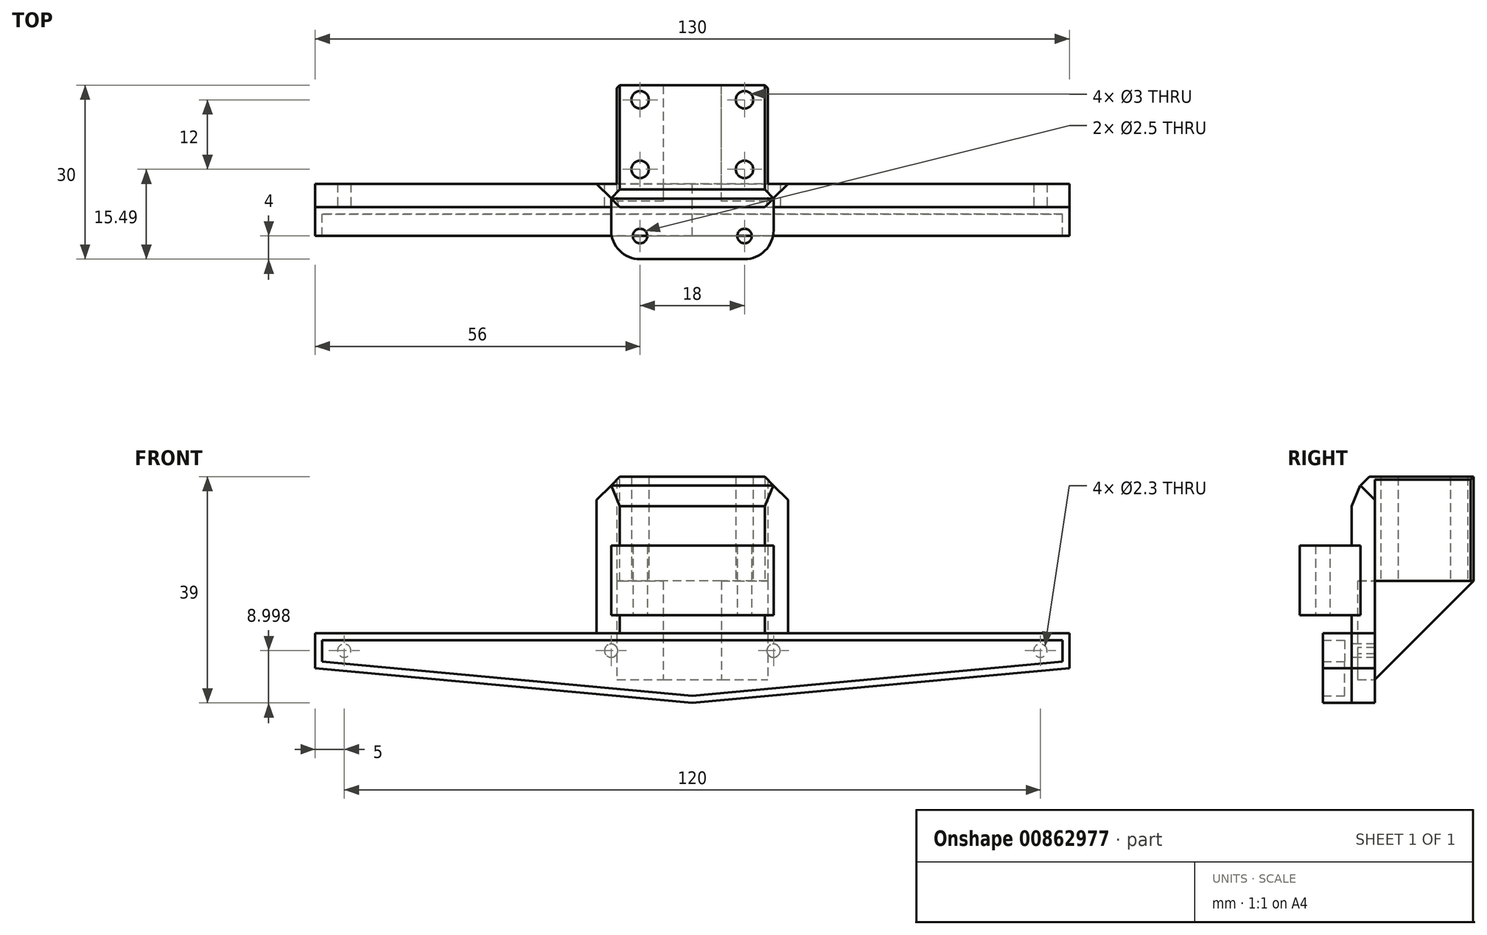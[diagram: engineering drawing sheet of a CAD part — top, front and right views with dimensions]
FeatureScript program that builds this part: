
annotation { "Feature Type Name" : "Feature", "Feature Type Description" : "" }
export const myFeature = defineFeature(function(context is Context, id is Id, definition is map)
    precondition{}
    {
        {
            var Q0;
            Q0=qCreatedBy(makeId("Top.planeOp"),FACE);
            var sketch = newSketch(context, id + "F0", { "sketchPlane" : qUnion([Q0])});
            skLineSegment(sketch, "E0.bottom", {"start": v(9, 10) * mm, "end": v(-9, 10) * mm});
            skLineSegment(sketch, "E0.top", {"start": v(9, -10) * mm, "end": v(-9, -10) * mm});
            skLineSegment(sketch, "E0.left", {"start": v(14, 5) * mm, "end": v(14, -5) * mm});
            skLineSegment(sketch, "E0.right", {"start": v(-14, 5) * mm, "end": v(-14, -5) * mm});
            skPoint(sketch, "E0.middle", {"position": v(0, 0) * mm});
            skCircle(sketch, "E1", {"center": v(-9, 6) * mm, "radius": 1.25 * mm});
            skCircle(sketch, "E2", {"center": v(9, 6) * mm, "radius": 1.25 * mm});
            skCircle(sketch, "E3", {"center": v(9, -6) * mm, "radius": 1.25 * mm});
            skCircle(sketch, "E4", {"center": v(-9, -6) * mm, "radius": 1.25 * mm});
            skPoint(sketch, "E5.visualSharp", {"position": v(-14, 10) * mm});
            skArc(sketch, "E5.filletArc", {"start": v(-9, 10) * mm, "mid": v(-12.54, 8.54) * mm, "end": v(-14, 5) * mm});
            skPoint(sketch, "E6.visualSharp", {"position": v(14, 10) * mm});
            skArc(sketch, "E6.filletArc", {"start": v(14, 5) * mm, "mid": v(12.54, 8.54) * mm, "end": v(9, 10) * mm});
            skPoint(sketch, "E7.visualSharp", {"position": v(14, -10) * mm});
            skArc(sketch, "E7.filletArc", {"start": v(9, -10) * mm, "mid": v(12.54, -8.54) * mm, "end": v(14, -5) * mm});
            skPoint(sketch, "E8.visualSharp", {"position": v(-14, -10) * mm});
            skArc(sketch, "E8.filletArc", {"start": v(-14, -5) * mm, "mid": v(-12.54, -8.54) * mm, "end": v(-9, -10) * mm});
            skSolve(sketch);
        }
        {
            var Q0;
            Q0 = qSketchRegion(id + "F0", true);
            extrude(context, id + "F1", {"entities" : qUnion([Q0]), "depth" : 12 * mm, "offsetDistance" : 25 * mm});
        }
        {
            var Q0;
            Q0=qCreatedBy(makeId("Front.planeOp"),FACE);
            var sketch = newSketch(context, id + "F2", { "sketchPlane" : qUnion([Q0])});
            skLineSegment(sketch, "E9", {"start": v(-65, -3.14) * mm, "end": v(65, -3.14) * mm});
            skLineSegment(sketch, "E10", {"start": v(65, -3.14) * mm, "end": v(65, -9.14) * mm});
            skLineSegment(sketch, "E11", {"start": v(65, -9.14) * mm, "end": v(0, -15.14) * mm});
            skLineSegment(sketch, "E12", {"start": v(0, -15.14) * mm, "end": v(-65, -9.14) * mm});
            skLineSegment(sketch, "E13", {"start": v(-65, -9.14) * mm, "end": v(-65, -3.14) * mm});
            skLineSegment(sketch, "E14", {"start": v(-17.48, -3.14) * mm, "end": v(-17.48, 23.86) * mm});
            skLineSegment(sketch, "E15", {"start": v(-17.48, 23.86) * mm, "end": v(17.48, 23.86) * mm});
            skLineSegment(sketch, "E16", {"start": v(17.48, 23.86) * mm, "end": v(17.48, -3.14) * mm});
            skLineSegment(sketch, "E17", {"start": v(-17.48, -3.14) * mm, "end": v(-17.48, -11.14) * mm});
            skLineSegment(sketch, "E18", {"start": v(-17.48, -11.14) * mm, "end": v(17.48, -11.14) * mm});
            skLineSegment(sketch, "E19", {"start": v(17.48, -11.14) * mm, "end": v(17.48, -3.14) * mm});
            skSolve(sketch);
        }
        {
            var Q0;
            Q0=makeQuery(id+"F2.imprint","IMPRINT",FACE,{"disambiguationData":[TD([[makeQuery(id+"F2.imprint","IMPRINT",EDGE,{"derivedFrom":sQuery(id+"F2.wireOp",EDGE,"E9")}),-1.0]])]});
            var Q1;
            {var subQ0=sQuery(id+"F2.wireOp",EDGE,"E14");Q1=makeQuery(id+"F2.imprint","IMPRINT",FACE,{"disambiguationData":[TD([[makeQuery(id+"F2.imprint","IMPRINT",EDGE,{"derivedFrom":subQ0}),-1.0]])]});}
            var Q2;
            {var subQ0=sQuery(id+"F2.wireOp",EDGE,"E17");Q2=makeQuery(id+"F2.imprint","IMPRINT",FACE,{"disambiguationData":[TD([[makeQuery(id+"F2.imprint","IMPRINT",EDGE,{"derivedFrom":subQ0}),1.0]])]});}
            extrude(context, id + "F3", {"entities" : qUnion([Q0, Q1, Q2]), "depth" : 1 * mm, "offsetDistance" : 25 * mm});
        }
        {
            var Q0;
            {var subQ0=sQuery(id+"F2.wireOp",EDGE,"E14");Q0=makeQuery(id+"F2.imprint","IMPRINT",FACE,{"disambiguationData":[TD([[makeQuery(id+"F2.imprint","IMPRINT",EDGE,{"derivedFrom":subQ0}),-1.0]])]});}
            var Q1;
            {var subQ0=sQuery(id+"F2.wireOp",EDGE,"E17");Q1=makeQuery(id+"F2.imprint","IMPRINT",FACE,{"disambiguationData":[TD([[makeQuery(id+"F2.imprint","IMPRINT",EDGE,{"derivedFrom":subQ0}),1.0]])]});}
            extrude(context, id + "F4", {"entities" : qUnion([Q0, Q1]), "operationType" : NewBodyOperationType.ADD, "oppositeDirection" : true, "depth" : 20 * mm, "offsetDistance" : 25 * mm});
        }
        {
            var Q0;
            Q0=makeQuery(id+"F3.opExtrude","CAP_FACE",FACE,{"disambiguationData":[OSD([sQuery(id+"F2.wireOp",EDGE,"E9"),sQuery(id+"F2.wireOp",EDGE,"E10"),sQuery(id+"F2.wireOp",EDGE,"E11"),sQuery(id+"F2.wireOp",EDGE,"E12"),sQuery(id+"F2.wireOp",EDGE,"E13"),sQuery(id+"F2.wireOp",EDGE,"E14"),sQuery(id+"F2.wireOp",EDGE,"E15"),sQuery(id+"F2.wireOp",EDGE,"E16")])],"isStart":false});
            var sketch = newSketch(context, id + "F5", { "sketchPlane" : qUnion([Q0])});
            skLineSegment(sketch, "E20", {"start": v(-65, -6.14) * mm, "end": v(65, -6.14) * mm, "construction": true});
            skCircle(sketch, "E21", {"center": v(-60, -6.14) * mm, "radius": 1.15 * mm});
            skCircle(sketch, "E22", {"center": v(60, -6.14) * mm, "radius": 1.15 * mm});
            skLineSegment(sketch, "E23", {"start": v(-55, -3.14) * mm, "end": v(-55, -10.06) * mm});
            skLineSegment(sketch, "E24", {"start": v(55, -3.14) * mm, "end": v(55, -10.06) * mm});
            skCircle(sketch, "E25", {"center": v(14, -6.14) * mm, "radius": 1.15 * mm});
            skCircle(sketch, "E26", {"center": v(-14, -6.14) * mm, "radius": 1.15 * mm});
            skSolve(sketch);
        }
        {
            var Q0;
            Q0=makeQuery(id+"F5.imprint","IMPRINT",FACE,{"disambiguationData":[TD([[makeQuery(id+"F5.imprint","IMPRINT",EDGE,{"derivedFrom":sQuery(id+"F5.wireOp",EDGE,"E21")}),-1.0]])]});
            var Q1;
            Q1=makeQuery(id+"F5.imprint","IMPRINT",FACE,{"disambiguationData":[TD([[makeQuery(id+"F5.imprint","IMPRINT",EDGE,{"derivedFrom":sQuery(id+"F5.wireOp",EDGE,"E22")}),-1.0]])]});
            var Q2;
            {var subQ0=sQuery(id+"F2.wireOp",EDGE,"E10");Q2=makeQuery(id+"F2.imprint","IMPRINT",FACE,{"disambiguationData":[TD([[makeQuery(id+"F2.imprint","IMPRINT",EDGE,{"derivedFrom":subQ0}),-1.0]])]});}
            extrude(context, id + "F6", {"entities" : qUnion([Q0, Q1, Q2]), "operationType" : NewBodyOperationType.ADD, "oppositeDirection" : true, "depth" : 3 * mm, "offsetDistance" : 25 * mm});
        }
        {
            var Q0;
            Q0=makeQuery(id+"F5.imprint","IMPRINT",FACE,{"disambiguationData":[TD([[makeQuery(id+"F5.imprint","IMPRINT",EDGE,{"derivedFrom":sQuery(id+"F5.wireOp",EDGE,"E21")}),1.0]])]});
            var Q1;
            Q1=makeQuery(id+"F5.imprint","IMPRINT",FACE,{"disambiguationData":[TD([[makeQuery(id+"F5.imprint","IMPRINT",EDGE,{"derivedFrom":sQuery(id+"F5.wireOp",EDGE,"E22")}),1.0]])]});
            extrude(context, id + "F7", {"entities" : qUnion([Q0, Q1]), "operationType" : NewBodyOperationType.REMOVE, "endBound" : BoundingType.UP_TO_NEXT, "oppositeDirection" : true, "depth" : 25 * mm, "offsetDistance" : 25 * mm});
        }
        {
            var Q0;
            Q0=makeQuery(id+"F5.imprint","IMPRINT",FACE,{"disambiguationData":[TD([[makeQuery(id+"F5.imprint","IMPRINT",EDGE,{"derivedFrom":sQuery(id+"F5.wireOp",EDGE,"E26")}),1.0]])]});
            var Q1;
            Q1=makeQuery(id+"F5.imprint","IMPRINT",FACE,{"disambiguationData":[TD([[makeQuery(id+"F5.imprint","IMPRINT",EDGE,{"derivedFrom":sQuery(id+"F5.wireOp",EDGE,"E25")}),1.0]])]});
            extrude(context, id + "F8", {"entities" : qUnion([Q0, Q1]), "operationType" : NewBodyOperationType.REMOVE, "oppositeDirection" : true, "depth" : 10 * mm, "offsetDistance" : 25 * mm});
        }
        {
            var Q0;
            Q0=makeQuery(id+"F4.opExtrude","SWEPT_FACE",FACE,{"disambiguationData":[OSD([sQuery(id+"F2.wireOp",EDGE,"E18")])]});
            var sketch = newSketch(context, id + "F9", { "sketchPlane" : qUnion([Q0])});
            skLineSegment(sketch, "E27", {"start": v(13, -20) * mm, "end": v(13, 0) * mm});
            skLineSegment(sketch, "E28", {"start": v(13, 0) * mm, "end": v(5, 0) * mm});
            skLineSegment(sketch, "E29", {"start": v(5, 0) * mm, "end": v(5, -20) * mm});
            skLineSegment(sketch, "E30", {"start": v(-5, -20) * mm, "end": v(-5, 0) * mm});
            skLineSegment(sketch, "E31", {"start": v(-5, 0) * mm, "end": v(-13, 0) * mm});
            skLineSegment(sketch, "E32", {"start": v(-13, 0) * mm, "end": v(-13, -20) * mm});
            skSolve(sketch);
        }
        {
            var Q0;
            {var subQ0=sQuery(id+"F9.wireOp",EDGE,"E27");Q0=makeQuery(id+"F9.imprint","IMPRINT",FACE,{"disambiguationData":[TD([[makeQuery(id+"F9.imprint","IMPRINT",EDGE,{"derivedFrom":subQ0}),1.0]])]});}
            var Q1;
            {var subQ0=sQuery(id+"F9.wireOp",EDGE,"E30");Q1=makeQuery(id+"F9.imprint","IMPRINT",FACE,{"disambiguationData":[TD([[makeQuery(id+"F9.imprint","IMPRINT",EDGE,{"derivedFrom":subQ0}),1.0]])]});}
            extrude(context, id + "F10", {"entities" : qUnion([Q0, Q1]), "operationType" : NewBodyOperationType.REMOVE, "oppositeDirection" : true, "depth" : 17 * mm, "offsetDistance" : 25 * mm});
        }
        {
            var Q0;
            Q0=makeQuery(id+"F10.boolean.opBoolean","COPY",FACE,{"derivedFrom":makeQuery(id+"F10.opExtrude","CAP_FACE",FACE,{"disambiguationData":[OSD([sQuery(id+"F2.wireOp",EDGE,"E18"),sQuery(id+"F9.wireOp",EDGE,"E30"),sQuery(id+"F9.wireOp",EDGE,"E31"),sQuery(id+"F9.wireOp",EDGE,"E32")])],"isStart":false})});
            var sketch = newSketch(context, id + "F11", { "sketchPlane" : qUnion([Q0])});
            skCircle(sketch, "E33", {"center": v(-9, -5.5) * mm, "radius": 1.5 * mm});
            skCircle(sketch, "E34", {"center": v(9, -5.5) * mm, "radius": 1.5 * mm});
            skCircle(sketch, "E35", {"center": v(9, -17.5) * mm, "radius": 1.5 * mm});
            skCircle(sketch, "E36", {"center": v(-9, -17.5) * mm, "radius": 1.5 * mm});
            skSolve(sketch);
        }
        {
            var Q0;
            Q0=makeQuery(id+"F11.imprint","IMPRINT",FACE,{"disambiguationData":[TD([[makeQuery(id+"F11.imprint","IMPRINT",EDGE,{"derivedFrom":sQuery(id+"F11.wireOp",EDGE,"E33")}),1.0]])]});
            var Q1;
            Q1=makeQuery(id+"F11.imprint","IMPRINT",FACE,{"disambiguationData":[TD([[makeQuery(id+"F11.imprint","IMPRINT",EDGE,{"derivedFrom":sQuery(id+"F11.wireOp",EDGE,"E36")}),1.0]])]});
            var Q2;
            Q2=makeQuery(id+"F11.imprint","IMPRINT",FACE,{"disambiguationData":[TD([[makeQuery(id+"F11.imprint","IMPRINT",EDGE,{"derivedFrom":sQuery(id+"F11.wireOp",EDGE,"E34")}),1.0]])]});
            var Q3;
            Q3=makeQuery(id+"F11.imprint","IMPRINT",FACE,{"disambiguationData":[TD([[makeQuery(id+"F11.imprint","IMPRINT",EDGE,{"derivedFrom":sQuery(id+"F11.wireOp",EDGE,"E35")}),1.0]])]});
            extrude(context, id + "F12", {"entities" : qUnion([Q0, Q1, Q2, Q3]), "operationType" : NewBodyOperationType.REMOVE, "endBound" : BoundingType.UP_TO_NEXT, "oppositeDirection" : true, "depth" : 25 * mm, "offsetDistance" : 25 * mm});
        }
        {
            var Q0;
            {var subQ4=sQuery(id+"F5.wireOp",EDGE,"E23");Q0=makeQuery(id+"F5.imprint","IMPRINT",FACE,{"disambiguationData":[TD([[makeQuery(id+"F5.imprint","IMPRINT",EDGE,{"derivedFrom":subQ4}),1.0]])]});}
            var sketch = newSketch(context, id + "F13", { "sketchPlane" : qUnion([Q0])});
            skLineSegment(sketch, "E37", {"start": v(-65, -2.43) * mm, "end": v(65, -2.43) * mm});
            skLineSegment(sketch, "E38", {"start": v(65, -2.43) * mm, "end": v(65, -8.43) * mm});
            skLineSegment(sketch, "E39", {"start": v(65, -8.43) * mm, "end": v(0, -14.43) * mm});
            skLineSegment(sketch, "E40", {"start": v(0, -14.43) * mm, "end": v(-65, -8.43) * mm});
            skLineSegment(sketch, "E41", {"start": v(-65, -8.43) * mm, "end": v(-65, -2.43) * mm});
            skSolve(sketch);
        }
        {
            var Q0;
            Q0 = qSketchRegion(id + "F13", true);
            extrude(context, id + "F14", {"entities" : qUnion([Q0]), "depth" : 5 * mm, "offsetDistance" : 25 * mm});
        }
        {
            var Q0;
            Q0=makeQuery(id+"F14.opExtrude","CAP_FACE",FACE,{"disambiguationData":[OSD([sQuery(id+"F13.wireOp",EDGE,"E37"),sQuery(id+"F13.wireOp",EDGE,"E38"),sQuery(id+"F13.wireOp",EDGE,"E39"),sQuery(id+"F13.wireOp",EDGE,"E40"),sQuery(id+"F13.wireOp",EDGE,"E41")])],"isStart":false});
            shell(context, id + "F15", {"entities" : qUnion([Q0]), "thickness" : 1.2 * mm});
        }
        {
            var Q0;
            Q0=makeQuery(id+"F15.opShell","OFFSET_FACE",FACE,{"disambiguationData":[OSD([sQuery(id+"F13.wireOp",EDGE,"E37"),sQuery(id+"F13.wireOp",EDGE,"E38"),sQuery(id+"F13.wireOp",EDGE,"E39"),sQuery(id+"F13.wireOp",EDGE,"E40"),sQuery(id+"F13.wireOp",EDGE,"E41")])]});
            extrude(context, id + "F16", {"entities" : qUnion([Q0]), "depth" : 3.8 * mm, "offsetDistance" : 25 * mm});
        }
        {
            var Q0;
            Q0=makeQuery(id+"F14.opExtrude","SWEPT_BODY",BODY,{"disambiguationData":[OSD([sQuery(id+"F13.wireOp",EDGE,"E37"),sQuery(id+"F13.wireOp",EDGE,"E38"),sQuery(id+"F13.wireOp",EDGE,"E39"),sQuery(id+"F13.wireOp",EDGE,"E40"),sQuery(id+"F13.wireOp",EDGE,"E41")])]});
            transform(context, id + "F17", {"entities" : qUnion([Q0]), "transformType" : TransformType.TRANSLATION_3D, "dx" : 0 * mm, "dy" : 0 * mm, "dz" : -0.7 * mm, "makeCopy" : false});
        }
        {
            var Q0;
            Q0=makeQuery(id+"F16.opExtrude","SWEPT_BODY",BODY,{"disambiguationData":[OSD([sQuery(id+"F13.wireOp",EDGE,"E37"),sQuery(id+"F13.wireOp",EDGE,"E38"),sQuery(id+"F13.wireOp",EDGE,"E39"),sQuery(id+"F13.wireOp",EDGE,"E40"),sQuery(id+"F13.wireOp",EDGE,"E41")])]});
            transform(context, id + "F18", {"entities" : qUnion([Q0]), "transformType" : TransformType.TRANSLATION_3D, "dx" : 0 * mm, "dy" : 0 * mm, "dz" : -0.7 * mm, "makeCopy" : false});
        }
        {
            var Q0;
            Q0=makeQuery(id+"F3.opExtrude","CAP_EDGE",EDGE,{"disambiguationData":[OSD([sQuery(id+"F2.wireOp",EDGE,"E14")])],"isStart":false});
            var Q1;
            Q1=makeQuery(id+"F3.opExtrude","CAP_EDGE",EDGE,{"disambiguationData":[OSD([sQuery(id+"F2.wireOp",EDGE,"E16")])],"isStart":false});
            var Q2;
            Q2=makeQuery(id+"F4.opExtrude","CAP_EDGE",EDGE,{"disambiguationData":[OSD([sQuery(id+"F2.wireOp",EDGE,"E14"),sQuery(id+"F2.wireOp",EDGE,"E17")])],"isStart":false});
            var Q3;
            Q3=makeQuery(id+"F4.opExtrude","CAP_EDGE",EDGE,{"disambiguationData":[OSD([sQuery(id+"F2.wireOp",EDGE,"E16"),sQuery(id+"F2.wireOp",EDGE,"E19")])],"isStart":false});
            var Q4;
            {var subQ0=sQuery(id+"F2.wireOp",EDGE,"E15");var subQ1=sQuery(id+"F2.wireOp",EDGE,"E14");Q4=makeQuery(id+"F4.boolean.opBoolean","MERGE",EDGE,{"derivedFrom":[makeQuery(id+"F3.opExtrude","SWEPT_EDGE",EDGE,{"disambiguationData":[OSD([subQ1,subQ0])]}),makeQuery(id+"F4.opExtrude","SWEPT_EDGE",EDGE,{"disambiguationData":[OSD([subQ1,subQ0])]})]});}
            var Q5;
            {var subQ0=sQuery(id+"F2.wireOp",EDGE,"E16");var subQ1=sQuery(id+"F2.wireOp",EDGE,"E15");Q5=makeQuery(id+"F4.boolean.opBoolean","MERGE",EDGE,{"derivedFrom":[makeQuery(id+"F3.opExtrude","SWEPT_EDGE",EDGE,{"disambiguationData":[OSD([subQ1,subQ0])]}),makeQuery(id+"F4.opExtrude","SWEPT_EDGE",EDGE,{"disambiguationData":[OSD([subQ1,subQ0])]})]});}
            chamfer(context, id + "F19", {"entities" : qUnion([Q0, Q1, Q2, Q3, Q4, Q5]), "width" : 5 * mm, "tangentPropagation" : true});
        }
        {
            var Q0;
            {var subQ0=sQuery(id+"F2.wireOp",EDGE,"E18");Q0=makeQuery(id+"F10.boolean.opBoolean","SPLIT",EDGE,{"disambiguationData":[TD([makeQuery(id+"F10.opExtrude","SWEPT_FACE",FACE,{"disambiguationData":[OSD([sQuery(id+"F9.wireOp",EDGE,"E29")])]})])],"derivedFrom":makeQuery(id+"F4.opExtrude","CAP_EDGE",EDGE,{"disambiguationData":[OSD([subQ0])],"isStart":false})});}
            chamfer(context, id + "F20", {"entities" : qUnion([Q0]), "width" : 17 * mm, "tangentPropagation" : true});
        }
        {
            var Q0;
            Q0=makeQuery(id+"F3.opExtrude","CAP_EDGE",EDGE,{"disambiguationData":[OSD([sQuery(id+"F2.wireOp",EDGE,"E15")])],"isStart":false});
            chamfer(context, id + "F21", {"entities" : qUnion([Q0]), "width" : 3 * mm, "tangentPropagation" : true});
        }
        {
            var Q0;
            {var subQ0=sQuery(id+"F2.wireOp",EDGE,"E15");Q0=makeQuery(id+"F21.opChamfer","BLEND_EDGE",EDGE,{"blendedFrom":[makeQuery(id+"F3.opExtrude","CAP_EDGE",EDGE,{"disambiguationData":[OSD([subQ0])],"isStart":false}),makeQuery(id+"F3.opExtrude","CAP_FACE",FACE,{"disambiguationData":[OSD([sQuery(id+"F2.wireOp",EDGE,"E9"),sQuery(id+"F2.wireOp",EDGE,"E10"),sQuery(id+"F2.wireOp",EDGE,"E11"),sQuery(id+"F2.wireOp",EDGE,"E12"),sQuery(id+"F2.wireOp",EDGE,"E13"),sQuery(id+"F2.wireOp",EDGE,"E14"),subQ0,sQuery(id+"F2.wireOp",EDGE,"E16")])],"isStart":false})],"blendedInto":[makeQuery(id+"F3.opExtrude","CAP_FACE",FACE,{"disambiguationData":[OSD([sQuery(id+"F2.wireOp",EDGE,"E9"),sQuery(id+"F2.wireOp",EDGE,"E10"),sQuery(id+"F2.wireOp",EDGE,"E11"),sQuery(id+"F2.wireOp",EDGE,"E12"),sQuery(id+"F2.wireOp",EDGE,"E13"),sQuery(id+"F2.wireOp",EDGE,"E14"),subQ0,sQuery(id+"F2.wireOp",EDGE,"E16")])],"isStart":false})]});}
            chamfer(context, id + "F22", {"entities" : qUnion([Q0]), "width" : 5 * mm, "tangentPropagation" : true});
        }
        {
            var Q0;
            {var subQ1=sQuery(id+"F2.wireOp",EDGE,"E18");var subQ3=sQuery(id+"F2.wireOp",EDGE,"E16");Q0=makeQuery(id+"F10.boolean.opBoolean","SPLIT",FACE,{"disambiguationData":[TD([makeQuery(id+"F3.opExtrude","SWEPT_FACE",FACE,{"disambiguationData":[OSD([subQ3])]})])],"derivedFrom":makeQuery(id+"F4.opExtrude","SWEPT_FACE",FACE,{"disambiguationData":[OSD([subQ1])]})});}
            var Q1;
            {var subQ1=sQuery(id+"F2.wireOp",EDGE,"E18");var subQ3=sQuery(id+"F2.wireOp",EDGE,"E14");Q1=makeQuery(id+"F10.boolean.opBoolean","SPLIT",FACE,{"disambiguationData":[TD([makeQuery(id+"F3.opExtrude","SWEPT_FACE",FACE,{"disambiguationData":[OSD([subQ3])]})])],"derivedFrom":makeQuery(id+"F4.opExtrude","SWEPT_FACE",FACE,{"disambiguationData":[OSD([subQ1])]})});}
            var Q2;
            {var subQ0=sQuery(id+"F2.wireOp",EDGE,"E15");Q2=makeQuery(id+"F4.boolean.opBoolean","MERGE",FACE,{"derivedFrom":[makeQuery(id+"F3.opExtrude","SWEPT_FACE",FACE,{"disambiguationData":[OSD([subQ0])]}),makeQuery(id+"F4.opExtrude","SWEPT_FACE",FACE,{"disambiguationData":[OSD([subQ0])]})]});}
            extrude(context, id + "F23", {"entities" : qUnion([Q0, Q1]), "operationType" : NewBodyOperationType.REMOVE, "endBound" : BoundingType.UP_TO_SURFACE, "oppositeDirection" : true, "depth" : 25 * mm, "endBoundEntityFace" : qUnion([Q2]), "offsetDistance" : 25 * mm});
        }
    });
